# Revit family: Hager-Univers-IP30-syst-Aufputz-CH-de
name_source: partatom
category: Electrical Equipment
units: mm (PartAtom-declared; Revit-internal decimal feet)

## family parameters
Cut with Voids When Loaded = No
Host = Face
Panel Configuration = Two Columns, Circuits Across
Part Type = Panelboard
Room Calculation Point = No
Round Connector Dimension = Use Diameter
Shared = No

## types (20) — shared parameters
EF000003 - Montageart = EV000384 - Aufputz
EF000007 - Farbe = EV000202 - weiß
EF000049 - Tiefe = 161 mm  [stored 0.528215 ft]
EF000116 - RAL-Nummer = 9010
EF000118 - Mit Montageplatte = No
EF000339 - Art der Abdeckung = EV000494 - ohne
EF001062 - EMV-Ausführung = No
EF001088 - Anbaumöglichkeit = Yes
EF001131 - Innentiefe = 161 mm  [stored 0.528215 ft]
EF001134 - DIN-Schiene = Yes
EF001596 - Werkstoff des Gehäuses = EV000179 - Stahl
EF002950 - Breite in Teilungseinheiten = 12
EF004462 - Art der Schließung = EV000154 - sonstige
EF005474 - Schutzart (IP) = EV006410 - IP30
EF006244 - Transparenter Deckel/Tür = No
EF006306 - Mit Schloss = No
EF009212 - Ausführung Deckel = EV009916 - mit Ausschnitt
EF015776 - Erdungsklemmenblock = Yes
EF015777 - Neutralleiterklemmenblock = Yes
EF015941 - Signaldurchlassende Tür = No
HG000002 - Mit tür = No
HG000003 - Bereich = Univers
HG000005 - Dicke = 3 mm  [stored 0.00984252 ft]
HG000006 - Unterputz = No
HG000009 - Doppelflügeligen Tür = No
HG000010 - Asymmetrische Türen = No
HG000011 - Leere Reihen von unten = No
HG000017 - Distanz zwischen den Polen = 18 mm  [stored 0.0590551 ft]
Manufacturer = Hager
Type Comments = Univers
zero-valued in all types: Default Elevation, EF000218 - Einbautiefe, EF000332 - Einbauhöhe, EF000846 - Einbaubreite, HG000007 - Anzahl der leeren Spalten, HG000008 - Anzahl der leeren Reihen

## per-type parameters (varying)
| type | EF000008 - Breite | EF000040 - Höhe | EF000266 - Anzahl der Reihen | HG000001 - Anzahl der Spalten | HG000004 - Herstellerreferenz | Model |
| Aufputz IP30 B1050 H1100 T161 12 Teilungseinheiten - FWB74T1S | 1050 mm | 1100 mm | 28 | 4 | FWB74T1S | FWB74T1S |
| Aufputz IP30 B1050 H500 T161 12 Teilungseinheiten - FWB34T1S | 1050 mm | 500 mm  [stored 1.64042 ft] | 12 | 4 | FWB34T1S | FWB34T1S |
| Aufputz IP30 B1050 H650 T161 12 Teilungseinheiten - FWB44T1S | 1050 mm | 650 mm  [stored 2.13255 ft] | 16 | 4 | FWB44T1S | FWB44T1S |
| Aufputz IP30 B1050 H800 T161 12 Teilungseinheiten - FWB54T1S | 1050 mm | 800 mm  [stored 2.62467 ft] | 20 | 4 | FWB54T1S | FWB54T1S |
| Aufputz IP30 B1050 H950 T161 12 Teilungseinheiten - FWB64T1S | 1050 mm | 950 mm  [stored 3.1168 ft] | 24 | 4 | FWB64T1S | FWB64T1S |
| Aufputz IP30 B300 H1100 T161 12 Teilungseinheiten - FWB71T1S | 300 mm | 1100 mm | 7 | 1 | FWB71T1S | FWB71T1S |
| Aufputz IP30 B300 H500 T161 12 Teilungseinheiten - FWB31T1S | 300 mm | 500 mm  [stored 1.64042 ft] | 3 | 1 | FWB31T1S | FWB31T1S |
| Aufputz IP30 B300 H650 T161 12 Teilungseinheiten - FWB41T1S | 300 mm | 650 mm  [stored 2.13255 ft] | 4 | 1 | FWB41T1S | FWB41T1S |
| Aufputz IP30 B300 H800 T161 12 Teilungseinheiten - FWB51T1S | 300 mm | 800 mm  [stored 2.62467 ft] | 5 | 1 | FWB51T1S | FWB51T1S |
| Aufputz IP30 B300 H950 T161 12 Teilungseinheiten - FWB61T1S | 300 mm | 950 mm  [stored 3.1168 ft] | 6 | 1 | FWB61T1S | FWB61T1S |
| Aufputz IP30 B550 H1100 T161 12 Teilungseinheiten - FWB72T1S | 550 mm | 1100 mm | 14 | 2 | FWB72T1S | FWB72T1S |
| Aufputz IP30 B550 H500 T161 12 Teilungseinheiten - FWB32T1S | 550 mm | 500 mm  [stored 1.64042 ft] | 6 | 2 | FWB32T1S | FWB32T1S |
| Aufputz IP30 B550 H650 T161 12 Teilungseinheiten - FWB42T1S | 550 mm | 650 mm  [stored 2.13255 ft] | 8 | 2 | FWB42T1S | FWB42T1S |
| Aufputz IP30 B550 H800 T161 12 Teilungseinheiten - FWB52T1S | 550 mm | 800 mm  [stored 2.62467 ft] | 10 | 2 | FWB52T1S | FWB52T1S |
| Aufputz IP30 B550 H950 T161 12 Teilungseinheiten - FWB62T1S | 550 mm | 950 mm  [stored 3.1168 ft] | 12 | 2 | FWB62T1S | FWB62T1S |
| Aufputz IP30 B800 H1100 T161 12 Teilungseinheiten - FWB73T1S | 800 mm  [stored 2.62467 ft] | 1100 mm | 21 | 3 | FWB73T1S | FWB73T1S |
| Aufputz IP30 B800 H500 T161 12 Teilungseinheiten - FWB33T1S | 800 mm  [stored 2.62467 ft] | 500 mm  [stored 1.64042 ft] | 9 | 3 | FWB33T1S | FWB33T1S |
| Aufputz IP30 B800 H650 T161 12 Teilungseinheiten - FWB43T1S | 800 mm  [stored 2.62467 ft] | 650 mm  [stored 2.13255 ft] | 12 | 3 | FWB43T1S | FWB43T1S |
| Aufputz IP30 B800 H800 T161 12 Teilungseinheiten - FWB53T1S | 800 mm  [stored 2.62467 ft] | 800 mm  [stored 2.62467 ft] | 15 | 3 | FWB53T1S | FWB53T1S |
| Aufputz IP30 B800 H950 T161 12 Teilungseinheiten - FWB63T1S | 800 mm  [stored 2.62467 ft] | 950 mm  [stored 3.1168 ft] | 18 | 3 | FWB63T1S | FWB63T1S |

note: [stored X ft] marks values corroborated as IEEE doubles in the binary element streams (Revit-internal decimal feet)

## geometry (parser evidence)
native form markers: Sweep x17
no freeform markers — native parametric forms only
